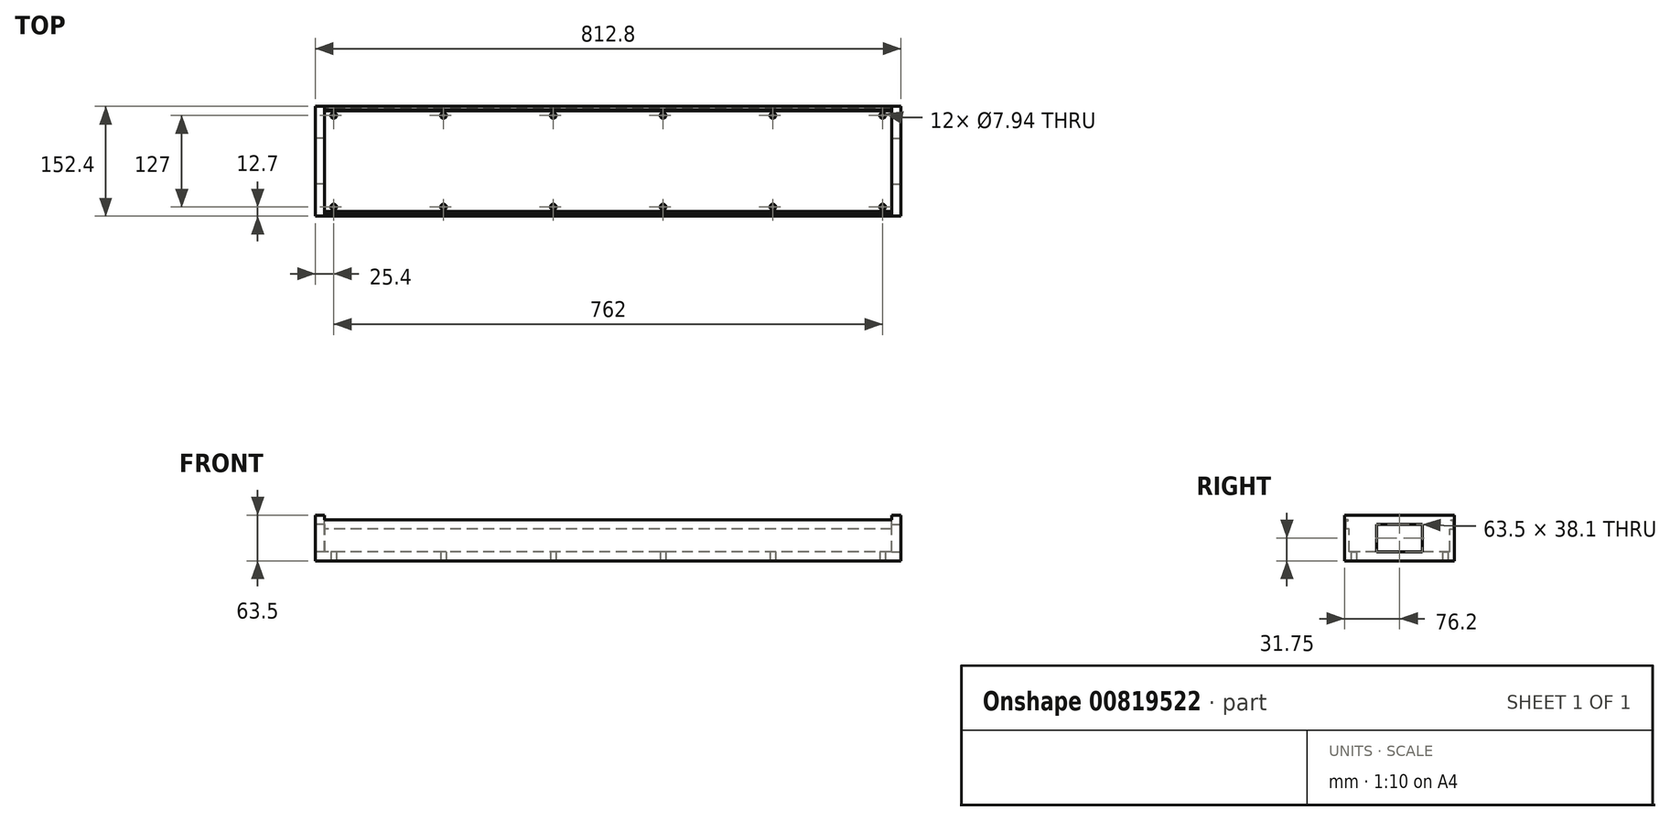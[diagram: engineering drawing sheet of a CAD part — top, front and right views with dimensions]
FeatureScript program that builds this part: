
annotation { "Feature Type Name" : "Feature", "Feature Type Description" : "" }
export const myFeature = defineFeature(function(context is Context, id is Id, definition is map)
    precondition{}
    {
        {
            var Q0;
            Q0=qCreatedBy(makeId("Top.planeOp"),FACE);
            var sketch = newSketch(context, id + "F0", { "sketchPlane" : qUnion([Q0])});
            skLineSegment(sketch, "E0.bottom", {"start": v(-406.4, 76.2) * mm, "end": v(406.4, 76.2) * mm});
            skLineSegment(sketch, "E0.top", {"start": v(-406.4, -76.2) * mm, "end": v(406.4, -76.2) * mm});
            skLineSegment(sketch, "E0.left", {"start": v(-406.4, 76.2) * mm, "end": v(-406.4, -76.2) * mm});
            skLineSegment(sketch, "E0.right", {"start": v(406.4, 76.2) * mm, "end": v(406.4, -76.2) * mm});
            skLineSegment(sketch, "E1", {"start": v(0, 76.2) * mm, "end": v(0, -76.2) * mm, "construction": true});
            skLineSegment(sketch, "E2", {"start": v(-406.4, 0) * mm, "end": v(406.4, 0) * mm, "construction": true});
            skCircle(sketch, "E3", {"center": v(381, 63.5) * mm, "radius": 3.97 * mm});
            skCircle(sketch, "E4", {"center": v(381, -63.5) * mm, "radius": 3.97 * mm});
            skLineSegment(sketch, "E5", {"start": v(381, 63.5) * mm, "end": v(381, 0) * mm, "construction": true});
            skLineSegment(sketch, "E6", {"start": v(381, 0) * mm, "end": v(381, -63.5) * mm, "construction": true});
            skCircle(sketch, "E7.1.0.0", {"center": v(228.6, 63.5) * mm, "radius": 3.97 * mm});
            skCircle(sketch, "E7.1.0.1", {"center": v(228.6, -63.5) * mm, "radius": 3.97 * mm});
            skCircle(sketch, "E7.2.0.0", {"center": v(76.2, 63.5) * mm, "radius": 3.97 * mm});
            skCircle(sketch, "E7.2.0.1", {"center": v(76.2, -63.5) * mm, "radius": 3.97 * mm});
            skCircle(sketch, "E7.3.0.0", {"center": v(-76.2, 63.5) * mm, "radius": 3.97 * mm});
            skCircle(sketch, "E7.3.0.1", {"center": v(-76.2, -63.5) * mm, "radius": 3.97 * mm});
            skCircle(sketch, "E7.4.0.0", {"center": v(-228.6, 63.5) * mm, "radius": 3.97 * mm});
            skCircle(sketch, "E7.4.0.1", {"center": v(-228.6, -63.5) * mm, "radius": 3.97 * mm});
            skCircle(sketch, "E7.5.0.0", {"center": v(-381, 63.5) * mm, "radius": 3.97 * mm});
            skCircle(sketch, "E7.5.0.1", {"center": v(-381, -63.5) * mm, "radius": 3.97 * mm});
            skLineSegment(sketch, "E7.direction1", {"start": v(381, 63.5) * mm, "end": v(228.6, 63.5) * mm, "construction": true});
            skSolve(sketch);
        }
        {
            var Q0;
            Q0=qSketchRegion(id+"F0",true);
            extrude(context, id + "F1", {"entities" : qUnion([Q0]), "depth" : 12.7 * mm, "offsetDistance" : 25.4 * mm});
        }
        {
            var Q0;
            Q0=makeQuery(id+"F1.opExtrude","SWEPT_FACE",FACE,{"disambiguationData":[OSD([sQuery(id+"F0.wireOp",EDGE,"E0.left")])]});
            var sketch = newSketch(context, id + "F2", { "sketchPlane" : qUnion([Q0])});
            skLineSegment(sketch, "E8.top", {"start": v(-76.2, 63.5) * mm, "end": v(76.2, 63.5) * mm});
            skLineSegment(sketch, "E8.left", {"start": v(-76.2, 12.7) * mm, "end": v(-76.2, 63.5) * mm});
            skLineSegment(sketch, "E8.right", {"start": v(76.2, 12.7) * mm, "end": v(76.2, 63.5) * mm});
            skLineSegment(sketch, "E9", {"start": v(-76.2, 12.7) * mm, "end": v(-31.75, 12.7) * mm});
            skLineSegment(sketch, "E10", {"start": v(-31.75, 12.7) * mm, "end": v(-31.75, 50.8) * mm});
            skLineSegment(sketch, "E11", {"start": v(-31.75, 50.8) * mm, "end": v(31.75, 50.8) * mm});
            skLineSegment(sketch, "E12", {"start": v(31.75, 50.8) * mm, "end": v(31.75, 12.7) * mm});
            skLineSegment(sketch, "E13", {"start": v(31.75, 12.7) * mm, "end": v(76.2, 12.7) * mm});
            skLineSegment(sketch, "E14", {"start": v(0, 50.8) * mm, "end": v(0, 12.7) * mm, "construction": true});
            skSolve(sketch);
        }
        {
            var Q0;
            Q0=qSketchRegion(id+"F2",true);
            extrude(context, id + "F3", {"entities" : qUnion([Q0]), "operationType" : NewBodyOperationType.ADD, "oppositeDirection" : true, "depth" : 12.7 * mm, "offsetDistance" : 25.4 * mm});
        }
        {
            var Q0;
            Q0=makeQuery(id+"F1.opExtrude","SWEPT_FACE",FACE,{"disambiguationData":[OSD([sQuery(id+"F0.wireOp",EDGE,"E0.right")])]});
            var sketch = newSketch(context, id + "F4", { "sketchPlane" : qUnion([Q0])});
            skLineSegment(sketch, "E15", {"start": v(-76.2, 12.7) * mm, "end": v(-76.2, 63.5) * mm});
            skLineSegment(sketch, "E16", {"start": v(-76.2, 63.5) * mm, "end": v(76.2, 63.5) * mm});
            skLineSegment(sketch, "E17", {"start": v(76.2, 63.5) * mm, "end": v(76.2, 12.7) * mm});
            skLineSegment(sketch, "E18", {"start": v(76.2, 12.7) * mm, "end": v(31.75, 12.7) * mm});
            skLineSegment(sketch, "E19", {"start": v(31.75, 12.7) * mm, "end": v(31.75, 50.8) * mm});
            skLineSegment(sketch, "E20", {"start": v(31.75, 50.8) * mm, "end": v(-31.75, 50.8) * mm});
            skLineSegment(sketch, "E21", {"start": v(-31.75, 50.8) * mm, "end": v(-31.75, 12.7) * mm});
            skLineSegment(sketch, "E22", {"start": v(-31.75, 12.7) * mm, "end": v(-76.2, 12.7) * mm});
            skSolve(sketch);
        }
        {
            var Q0;
            Q0=makeQuery(id+"F4.imprint","IMPRINT",FACE,{"disambiguationData":[TD([[makeQuery(id+"F4.imprint","IMPRINT",EDGE,{"derivedFrom":sQuery(id+"F4.wireOp",EDGE,"E15")}),-1.0]])]});
            extrude(context, id + "F5", {"entities" : qUnion([Q0]), "operationType" : NewBodyOperationType.ADD, "oppositeDirection" : true, "depth" : 12.7 * mm, "offsetDistance" : 25.4 * mm});
        }
        {
            var Q0;
            Q0=qCreatedBy(makeId("Right.planeOp"),FACE);
            var sketch = newSketch(context, id + "F6", { "sketchPlane" : qUnion([Q0])});
            skLineSegment(sketch, "E23", {"start": v(76.2, 12.7) * mm, "end": v(69.85, 12.7) * mm});
            skLineSegment(sketch, "E24", {"start": v(69.85, 44.45) * mm, "end": v(74.61, 44.45) * mm});
            skLineSegment(sketch, "E25", {"start": v(74.61, 44.45) * mm, "end": v(74.61, 55.56) * mm});
            skLineSegment(sketch, "E26", {"start": v(74.61, 55.56) * mm, "end": v(71.44, 55.56) * mm});
            skLineSegment(sketch, "E27", {"start": v(71.44, 57.15) * mm, "end": v(76.2, 57.15) * mm});
            skLineSegment(sketch, "E28", {"start": v(76.2, 57.15) * mm, "end": v(76.2, 12.7) * mm});
            skLineSegment(sketch, "E29", {"start": v(74.61, 44.45) * mm, "end": v(76.2, 44.45) * mm, "construction": true});
            skLineSegment(sketch, "E30.MirrorCS", {"start": v(-76.2, 57.15) * mm, "end": v(-76.2, 12.7) * mm});
            skLineSegment(sketch, "E31.MirrorCS", {"start": v(-71.44, 57.15) * mm, "end": v(-76.2, 57.15) * mm});
            skLineSegment(sketch, "E32.MirrorCS", {"start": v(-71.44, 55.56) * mm, "end": v(-71.44, 57.15) * mm});
            skLineSegment(sketch, "E33.MirrorCS", {"start": v(-74.61, 55.56) * mm, "end": v(-71.44, 55.56) * mm});
            skLineSegment(sketch, "E34.MirrorCS", {"start": v(-74.61, 44.45) * mm, "end": v(-74.61, 55.56) * mm});
            skLineSegment(sketch, "E35.MirrorCS", {"start": v(-69.85, 44.45) * mm, "end": v(-74.61, 44.45) * mm});
            skLineSegment(sketch, "E36.MirrorCS", {"start": v(-69.85, 12.7) * mm, "end": v(-69.85, 44.45) * mm});
            skLineSegment(sketch, "E37.MirrorCS", {"start": v(-76.2, 12.7) * mm, "end": v(-69.85, 12.7) * mm});
            skLineSegment(sketch, "E38", {"start": v(69.85, 12.7) * mm, "end": v(69.85, 44.45) * mm});
            skLineSegment(sketch, "E39", {"start": v(71.44, 55.56) * mm, "end": v(71.44, 57.15) * mm});
            skSolve(sketch);
        }
        {
            var Q0;
            Q0=qSketchRegion(id+"F6",true);
            extrude(context, id + "F7", {"entities" : qUnion([Q0]), "operationType" : NewBodyOperationType.ADD, "endBound" : BoundingType.SYMMETRIC, "depth" : 787.4 * mm, "offsetDistance" : 25.4 * mm});
        }
    });
